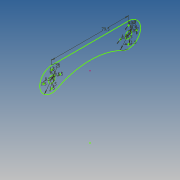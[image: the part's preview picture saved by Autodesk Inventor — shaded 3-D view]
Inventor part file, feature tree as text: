
AUTODESK INVENTOR PART (.ipt)
format: ipt  version: 2014 (Build 180170000, 170)  size: 80,896 bytes
history: native  units: mm
features: sketch x1
ambient origin geometry x8: Origin, YZ Plane, XZ Plane, XY Plane, X Axis, Y Axis, Z Axis, Center Point
feature tree (1):
  sketch  "Sketch1"  dims[d0=79.5mm d2=25.0mm d3=25.0mm d5=7.0mm d6=1.5mm d7=1.5mm d9=1.5mm d11=8.5mm d12=8.5mm d13=8.5mm d15=1.5mm d16=8.5mm d18=7.0mm d19=1.5mm d20=1.5mm d21=1.5mm d22=1.5mm d23=8.5mm d24=8.5mm d25=8.5mm d26=8.5mm]
